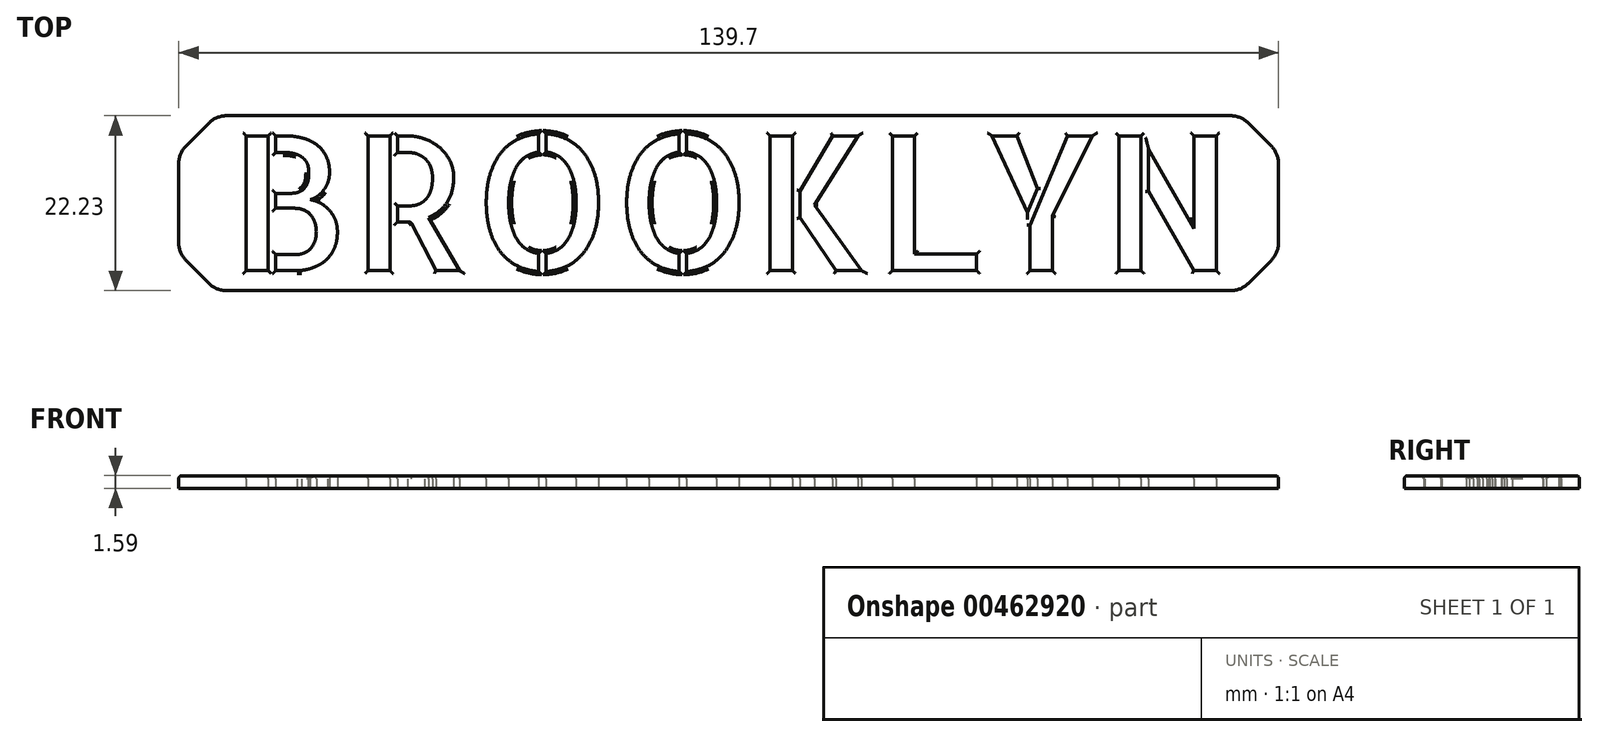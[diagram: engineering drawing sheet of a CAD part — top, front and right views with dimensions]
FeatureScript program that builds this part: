
annotation { "Feature Type Name" : "Feature", "Feature Type Description" : "" }
export const myFeature = defineFeature(function(context is Context, id is Id, definition is map)
    precondition{}
    {
        {
            var Q0;
            Q0=qCreatedBy(makeId("Top.planeOp"),FACE);
            var sketch = newSketch(context, id + "F0", { "sketchPlane" : qUnion([Q0])});
            skText(sketch, "E0", { "text": "BROOKLYN", "fontName": "AllertaStencil-Regular.ttf"});
            skLineSegment(sketch, "E1.bottom", {"start": v(-6.35, 19.68) * mm, "end": v(133.35, 19.68) * mm});
            skLineSegment(sketch, "E1.top", {"start": v(-6.35, -2.55) * mm, "end": v(133.35, -2.55) * mm});
            skLineSegment(sketch, "E1.left", {"start": v(-6.35, 19.68) * mm, "end": v(-6.35, -2.55) * mm});
            skLineSegment(sketch, "E1.right", {"start": v(133.35, 19.68) * mm, "end": v(133.35, -2.55) * mm});
            skLineSegment(sketch, "E2", {"start": v(63.5, 17.13) * mm, "end": v(63.5, 19.68) * mm, "construction": true});
            skLineSegment(sketch, "E3", {"start": v(63.5, -2.55) * mm, "end": v(63.5, 0) * mm, "construction": true});
            const initialGuessF0  = {"E0": [0, 0, 1, 0, 0.01713]};
            skSetInitialGuess(sketch, initialGuessF0);
            skSolve(sketch);
        }
        {
            var Q0;
            Q0 = qSketchRegion(id + "F0", true);
            extrude(context, id + "F1", {"entities" : qUnion([Q0]), "depth" : 1.59 * mm});
        }
        {
            var Q0;
            Q0=makeQuery(id+"F1.opExtrude","SWEPT_EDGE",EDGE,{"disambiguationData":[OSD([sQuery(id+"F0.wireOp",EDGE,"E1.bottom"),sQuery(id+"F0.wireOp",EDGE,"E1.right")])]});
            var Q1;
            Q1=makeQuery(id+"F1.opExtrude","SWEPT_EDGE",EDGE,{"disambiguationData":[OSD([sQuery(id+"F0.wireOp",EDGE,"E1.top"),sQuery(id+"F0.wireOp",EDGE,"E1.right")])]});
            var Q2;
            Q2=makeQuery(id+"F1.opExtrude","SWEPT_EDGE",EDGE,{"disambiguationData":[OSD([sQuery(id+"F0.wireOp",EDGE,"E1.top"),sQuery(id+"F0.wireOp",EDGE,"E1.left")])]});
            var Q3;
            Q3=makeQuery(id+"F1.opExtrude","SWEPT_EDGE",EDGE,{"disambiguationData":[OSD([sQuery(id+"F0.wireOp",EDGE,"E1.bottom"),sQuery(id+"F0.wireOp",EDGE,"E1.left")])]});
            chamfer(context, id + "F2", {"entities" : qUnion([Q0, Q1, Q2, Q3]), "width" : 4.76 * mm, "tangentPropagation" : true});
        }
        {
            var Q0;
            Q0=makeQuery(id+"F1.opExtrude","CAP_EDGE",EDGE,{"disambiguationData":[OSD([sQuery(id+"F0.wireOp",EDGE,"E0.sketch_text.stroke-179")])],"isStart":false});
            var Q1;
            Q1=makeQuery(id+"F1.opExtrude","CAP_EDGE",EDGE,{"disambiguationData":[OSD([sQuery(id+"F0.wireOp",EDGE,"E0.sketch_text.stroke-182")])],"isStart":false});
            var Q2;
            Q2=makeQuery(id+"F1.opExtrude","CAP_EDGE",EDGE,{"disambiguationData":[OSD([sQuery(id+"F0.wireOp",EDGE,"E0.sketch_text.stroke-181")])],"isStart":false});
            var Q3;
            Q3=makeQuery(id+"F1.opExtrude","CAP_EDGE",EDGE,{"disambiguationData":[OSD([sQuery(id+"F0.wireOp",EDGE,"E0.sketch_text.stroke-180")])],"isStart":false});
            fillet(context, id + "F3", {"entities" : qUnion([Q0, Q1, Q2, Q3]), "radius" : 0.38 * mm, "tangentPropagation" : true, "allowEdgeOverflow" : false});
        }
        {
            var Q0;
            Q0=makeQuery(id+"F1.opExtrude","CAP_EDGE",EDGE,{"disambiguationData":[OSD([sQuery(id+"F0.wireOp",EDGE,"E0.sketch_text.stroke-177")])],"isStart":false});
            var Q1;
            Q1=makeQuery(id+"F1.opExtrude","CAP_EDGE",EDGE,{"disambiguationData":[OSD([sQuery(id+"F0.wireOp",EDGE,"E0.sketch_text.stroke-175")])],"isStart":false});
            var Q2;
            Q2=makeQuery(id+"F1.opExtrude","CAP_EDGE",EDGE,{"disambiguationData":[OSD([sQuery(id+"F0.wireOp",EDGE,"E0.sketch_text.stroke-176")])],"isStart":false});
            var Q3;
            Q3=makeQuery(id+"F1.opExtrude","CAP_EDGE",EDGE,{"disambiguationData":[OSD([sQuery(id+"F0.wireOp",EDGE,"E0.sketch_text.stroke-178")])],"isStart":false});
            var Q4;
            Q4=makeQuery(id+"F1.opExtrude","CAP_EDGE",EDGE,{"disambiguationData":[OSD([sQuery(id+"F0.wireOp",EDGE,"E0.sketch_text.stroke-172")])],"isStart":false});
            var Q5;
            Q5=makeQuery(id+"F1.opExtrude","CAP_EDGE",EDGE,{"disambiguationData":[OSD([sQuery(id+"F0.wireOp",EDGE,"E0.sketch_text.stroke-173")])],"isStart":false});
            var Q6;
            Q6=makeQuery(id+"F1.opExtrude","CAP_EDGE",EDGE,{"disambiguationData":[OSD([sQuery(id+"F0.wireOp",EDGE,"E0.sketch_text.stroke-174")])],"isStart":false});
            var Q7;
            Q7=makeQuery(id+"F1.opExtrude","CAP_EDGE",EDGE,{"disambiguationData":[OSD([sQuery(id+"F0.wireOp",EDGE,"E0.sketch_text.stroke-163")])],"isStart":false});
            var Q8;
            Q8=makeQuery(id+"F1.opExtrude","CAP_EDGE",EDGE,{"disambiguationData":[OSD([sQuery(id+"F0.wireOp",EDGE,"E0.sketch_text.stroke-164")])],"isStart":false});
            var Q9;
            Q9=makeQuery(id+"F1.opExtrude","CAP_EDGE",EDGE,{"disambiguationData":[OSD([sQuery(id+"F0.wireOp",EDGE,"E0.sketch_text.stroke-165")])],"isStart":false});
            var Q10;
            Q10=makeQuery(id+"F1.opExtrude","CAP_EDGE",EDGE,{"disambiguationData":[OSD([sQuery(id+"F0.wireOp",EDGE,"E0.sketch_text.stroke-166")])],"isStart":false});
            var Q11;
            Q11=makeQuery(id+"F1.opExtrude","CAP_EDGE",EDGE,{"disambiguationData":[OSD([sQuery(id+"F0.wireOp",EDGE,"E0.sketch_text.stroke-167")])],"isStart":false});
            var Q12;
            Q12=makeQuery(id+"F1.opExtrude","CAP_EDGE",EDGE,{"disambiguationData":[OSD([sQuery(id+"F0.wireOp",EDGE,"E0.sketch_text.stroke-162")])],"isStart":false});
            var Q13;
            Q13=makeQuery(id+"F1.opExtrude","CAP_EDGE",EDGE,{"disambiguationData":[OSD([sQuery(id+"F0.wireOp",EDGE,"E0.sketch_text.stroke-168")])],"isStart":false});
            var Q14;
            Q14=makeQuery(id+"F1.opExtrude","CAP_EDGE",EDGE,{"disambiguationData":[OSD([sQuery(id+"F0.wireOp",EDGE,"E0.sketch_text.stroke-171")])],"isStart":false});
            var Q15;
            Q15=makeQuery(id+"F1.opExtrude","CAP_EDGE",EDGE,{"disambiguationData":[OSD([sQuery(id+"F0.wireOp",EDGE,"E0.sketch_text.stroke-170")])],"isStart":false});
            var Q16;
            Q16=makeQuery(id+"F1.opExtrude","CAP_EDGE",EDGE,{"disambiguationData":[OSD([sQuery(id+"F0.wireOp",EDGE,"E0.sketch_text.stroke-169")])],"isStart":false});
            fillet(context, id + "F4", {"entities" : qUnion([Q0, Q1, Q2, Q3, Q4, Q5, Q6, Q7, Q8, Q9, Q10, Q11, Q12, Q13, Q14, Q15, Q16]), "radius" : 0.38 * mm, "tangentPropagation" : true, "allowEdgeOverflow" : false});
        }
        {
            var Q0;
            Q0=makeQuery(id+"F1.opExtrude","CAP_EDGE",EDGE,{"disambiguationData":[OSD([sQuery(id+"F0.wireOp",EDGE,"E0.sketch_text.stroke-157")])],"isStart":false});
            var Q1;
            Q1=makeQuery(id+"F1.opExtrude","CAP_EDGE",EDGE,{"disambiguationData":[OSD([sQuery(id+"F0.wireOp",EDGE,"E0.sketch_text.stroke-156")])],"isStart":false});
            var Q2;
            Q2=makeQuery(id+"F1.opExtrude","CAP_EDGE",EDGE,{"disambiguationData":[OSD([sQuery(id+"F0.wireOp",EDGE,"E0.sketch_text.stroke-161")])],"isStart":false});
            var Q3;
            Q3=makeQuery(id+"F1.opExtrude","CAP_EDGE",EDGE,{"disambiguationData":[OSD([sQuery(id+"F0.wireOp",EDGE,"E0.sketch_text.stroke-160")])],"isStart":false});
            var Q4;
            Q4=makeQuery(id+"F1.opExtrude","CAP_EDGE",EDGE,{"disambiguationData":[OSD([sQuery(id+"F0.wireOp",EDGE,"E0.sketch_text.stroke-159")])],"isStart":false});
            var Q5;
            Q5=makeQuery(id+"F1.opExtrude","CAP_EDGE",EDGE,{"disambiguationData":[OSD([sQuery(id+"F0.wireOp",EDGE,"E0.sketch_text.stroke-158")])],"isStart":false});
            var Q6;
            Q6=makeQuery(id+"F1.opExtrude","CAP_EDGE",EDGE,{"disambiguationData":[OSD([sQuery(id+"F0.wireOp",EDGE,"E0.sketch_text.stroke-150")])],"isStart":false});
            var Q7;
            Q7=makeQuery(id+"F1.opExtrude","CAP_EDGE",EDGE,{"disambiguationData":[OSD([sQuery(id+"F0.wireOp",EDGE,"E0.sketch_text.stroke-149")])],"isStart":false});
            var Q8;
            Q8=makeQuery(id+"F1.opExtrude","CAP_EDGE",EDGE,{"disambiguationData":[OSD([sQuery(id+"F0.wireOp",EDGE,"E0.sketch_text.stroke-151")])],"isStart":false});
            var Q9;
            Q9=makeQuery(id+"F1.opExtrude","CAP_EDGE",EDGE,{"disambiguationData":[OSD([sQuery(id+"F0.wireOp",EDGE,"E0.sketch_text.stroke-155")])],"isStart":false});
            var Q10;
            Q10=makeQuery(id+"F1.opExtrude","CAP_EDGE",EDGE,{"disambiguationData":[OSD([sQuery(id+"F0.wireOp",EDGE,"E0.sketch_text.stroke-152")])],"isStart":false});
            var Q11;
            Q11=makeQuery(id+"F1.opExtrude","CAP_EDGE",EDGE,{"disambiguationData":[OSD([sQuery(id+"F0.wireOp",EDGE,"E0.sketch_text.stroke-153")])],"isStart":false});
            var Q12;
            Q12=makeQuery(id+"F1.opExtrude","CAP_EDGE",EDGE,{"disambiguationData":[OSD([sQuery(id+"F0.wireOp",EDGE,"E0.sketch_text.stroke-154")])],"isStart":false});
            var Q13;
            Q13=makeQuery(id+"F1.opExtrude","CAP_EDGE",EDGE,{"disambiguationData":[OSD([sQuery(id+"F0.wireOp",EDGE,"E0.sketch_text.stroke-145")])],"isStart":false});
            var Q14;
            Q14=makeQuery(id+"F1.opExtrude","CAP_EDGE",EDGE,{"disambiguationData":[OSD([sQuery(id+"F0.wireOp",EDGE,"E0.sketch_text.stroke-147")])],"isStart":false});
            var Q15;
            Q15=makeQuery(id+"F1.opExtrude","CAP_EDGE",EDGE,{"disambiguationData":[OSD([sQuery(id+"F0.wireOp",EDGE,"E0.sketch_text.stroke-148")])],"isStart":false});
            var Q16;
            Q16=makeQuery(id+"F1.opExtrude","CAP_EDGE",EDGE,{"disambiguationData":[OSD([sQuery(id+"F0.wireOp",EDGE,"E0.sketch_text.stroke-146")])],"isStart":false});
            fillet(context, id + "F5", {"entities" : qUnion([Q0, Q1, Q2, Q3, Q4, Q5, Q6, Q7, Q8, Q9, Q10, Q11, Q12, Q13, Q14, Q15, Q16]), "radius" : 0.38 * mm, "tangentPropagation" : true, "allowEdgeOverflow" : false});
        }
        {
            var Q0;
            Q0=makeQuery(id+"F1.opExtrude","CAP_EDGE",EDGE,{"disambiguationData":[OSD([sQuery(id+"F0.wireOp",EDGE,"E0.sketch_text.stroke-42")])],"isStart":false});
            var Q1;
            Q1=makeQuery(id+"F1.opExtrude","CAP_EDGE",EDGE,{"disambiguationData":[OSD([sQuery(id+"F0.wireOp",EDGE,"E0.sketch_text.stroke-40")])],"isStart":false});
            var Q2;
            Q2=makeQuery(id+"F1.opExtrude","CAP_EDGE",EDGE,{"disambiguationData":[OSD([sQuery(id+"F0.wireOp",EDGE,"E0.sketch_text.stroke-39")])],"isStart":false});
            var Q3;
            Q3=makeQuery(id+"F1.opExtrude","CAP_EDGE",EDGE,{"disambiguationData":[OSD([sQuery(id+"F0.wireOp",EDGE,"E0.sketch_text.stroke-41")])],"isStart":false});
            var Q4;
            Q4=makeQuery(id+"F1.opExtrude","CAP_EDGE",EDGE,{"disambiguationData":[OSD([sQuery(id+"F0.wireOp",EDGE,"E0.sketch_text.stroke-46")])],"isStart":false});
            var Q5;
            Q5=makeQuery(id+"F1.opExtrude","CAP_EDGE",EDGE,{"disambiguationData":[OSD([sQuery(id+"F0.wireOp",EDGE,"E0.sketch_text.stroke-43")])],"isStart":false});
            var Q6;
            Q6=makeQuery(id+"F1.opExtrude","CAP_EDGE",EDGE,{"disambiguationData":[OSD([sQuery(id+"F0.wireOp",EDGE,"E0.sketch_text.stroke-44")])],"isStart":false});
            var Q7;
            Q7=makeQuery(id+"F1.opExtrude","CAP_EDGE",EDGE,{"disambiguationData":[OSD([sQuery(id+"F0.wireOp",EDGE,"E0.sketch_text.stroke-45")])],"isStart":false});
            fillet(context, id + "F6", {"entities" : qUnion([Q0, Q1, Q2, Q3, Q4, Q5, Q6, Q7]), "radius" : 0.38 * mm, "tangentPropagation" : true, "allowEdgeOverflow" : false});
        }
        {
            var Q0;
            Q0=makeQuery(id+"F1.opExtrude","CAP_EDGE",EDGE,{"disambiguationData":[OSD([sQuery(id+"F0.wireOp",EDGE,"E0.sketch_text.stroke-17")])],"isStart":false});
            var Q1;
            Q1=makeQuery(id+"F1.opExtrude","CAP_EDGE",EDGE,{"disambiguationData":[OSD([sQuery(id+"F0.wireOp",EDGE,"E0.sketch_text.stroke-11")])],"isStart":false});
            var Q2;
            Q2=makeQuery(id+"F1.opExtrude","CAP_EDGE",EDGE,{"disambiguationData":[OSD([sQuery(id+"F0.wireOp",EDGE,"E0.sketch_text.stroke-10")])],"isStart":false});
            var Q3;
            Q3=makeQuery(id+"F1.opExtrude","CAP_EDGE",EDGE,{"disambiguationData":[OSD([sQuery(id+"F0.wireOp",EDGE,"E0.sketch_text.stroke-37")])],"isStart":false});
            var Q4;
            Q4=makeQuery(id+"F1.opExtrude","CAP_EDGE",EDGE,{"disambiguationData":[OSD([sQuery(id+"F0.wireOp",EDGE,"E0.sketch_text.stroke-29")])],"isStart":false});
            var Q5;
            Q5=makeQuery(id+"F1.opExtrude","CAP_EDGE",EDGE,{"disambiguationData":[OSD([sQuery(id+"F0.wireOp",EDGE,"E0.sketch_text.stroke-28")])],"isStart":false});
            var Q6;
            Q6=makeQuery(id+"F1.opExtrude","CAP_EDGE",EDGE,{"disambiguationData":[OSD([sQuery(id+"F0.wireOp",EDGE,"E0.sketch_text.stroke-18")])],"isStart":false});
            fillet(context, id + "F7", {"entities" : qUnion([Q0, Q1, Q2, Q3, Q4, Q5, Q6]), "radius" : 0.38 * mm, "tangentPropagation" : true, "allowEdgeOverflow" : false});
        }
        {
            var Q0;
            Q0=makeQuery(id+"F1.opExtrude","CAP_EDGE",EDGE,{"disambiguationData":[OSD([sQuery(id+"F0.wireOp",EDGE,"E0.sketch_text.stroke-53")])],"isStart":false});
            var Q1;
            Q1=makeQuery(id+"F1.opExtrude","CAP_EDGE",EDGE,{"disambiguationData":[OSD([sQuery(id+"F0.wireOp",EDGE,"E0.sketch_text.stroke-54")])],"isStart":false});
            var Q2;
            Q2=makeQuery(id+"F1.opExtrude","CAP_EDGE",EDGE,{"disambiguationData":[OSD([sQuery(id+"F0.wireOp",EDGE,"E0.sketch_text.stroke-64")])],"isStart":false});
            var Q3;
            Q3=makeQuery(id+"F1.opExtrude","CAP_EDGE",EDGE,{"disambiguationData":[OSD([sQuery(id+"F0.wireOp",EDGE,"E0.sketch_text.stroke-65")])],"isStart":false});
            var Q4;
            Q4=makeQuery(id+"F1.opExtrude","CAP_EDGE",EDGE,{"disambiguationData":[OSD([sQuery(id+"F0.wireOp",EDGE,"E0.sketch_text.stroke-72")])],"isStart":false});
            var Q5;
            Q5=makeQuery(id+"F1.opExtrude","CAP_EDGE",EDGE,{"disambiguationData":[OSD([sQuery(id+"F0.wireOp",EDGE,"E0.sketch_text.stroke-47")])],"isStart":false});
            var Q6;
            Q6=makeQuery(id+"F1.opExtrude","CAP_EDGE",EDGE,{"disambiguationData":[OSD([sQuery(id+"F0.wireOp",EDGE,"E0.sketch_text.stroke-48")])],"isStart":false});
            fillet(context, id + "F8", {"entities" : qUnion([Q0, Q1, Q2, Q3, Q4, Q5, Q6]), "radius" : 0.38 * mm, "tangentPropagation" : true, "allowEdgeOverflow" : false});
        }
        {
            var Q0;
            Q0=makeQuery(id+"F1.opExtrude","CAP_EDGE",EDGE,{"disambiguationData":[OSD([sQuery(id+"F0.wireOp",EDGE,"E0.sketch_text.stroke-52")])],"isStart":false});
            var Q1;
            Q1=makeQuery(id+"F1.opExtrude","CAP_EDGE",EDGE,{"disambiguationData":[OSD([sQuery(id+"F0.wireOp",EDGE,"E0.sketch_text.stroke-76")])],"isStart":false});
            var Q2;
            Q2=makeQuery(id+"F1.opExtrude","CAP_EDGE",EDGE,{"disambiguationData":[OSD([sQuery(id+"F0.wireOp",EDGE,"E0.sketch_text.stroke-86")])],"isStart":false});
            var Q3;
            Q3=makeQuery(id+"F1.opExtrude","CAP_EDGE",EDGE,{"disambiguationData":[OSD([sQuery(id+"F0.wireOp",EDGE,"E0.sketch_text.stroke-85")])],"isStart":false});
            var Q4;
            Q4=makeQuery(id+"F1.opExtrude","CAP_EDGE",EDGE,{"disambiguationData":[OSD([sQuery(id+"F0.wireOp",EDGE,"E0.sketch_text.stroke-81")])],"isStart":false});
            var Q5;
            Q5=makeQuery(id+"F1.opExtrude","CAP_EDGE",EDGE,{"disambiguationData":[OSD([sQuery(id+"F0.wireOp",EDGE,"E0.sketch_text.stroke-77")])],"isStart":false});
            var Q6;
            Q6=makeQuery(id+"F1.opExtrude","CAP_EDGE",EDGE,{"disambiguationData":[OSD([sQuery(id+"F0.wireOp",EDGE,"E0.sketch_text.stroke-108")])],"isStart":false});
            var Q7;
            Q7=makeQuery(id+"F1.opExtrude","CAP_EDGE",EDGE,{"disambiguationData":[OSD([sQuery(id+"F0.wireOp",EDGE,"E0.sketch_text.stroke-107")])],"isStart":false});
            var Q8;
            Q8=makeQuery(id+"F1.opExtrude","CAP_EDGE",EDGE,{"disambiguationData":[OSD([sQuery(id+"F0.wireOp",EDGE,"E0.sketch_text.stroke-103")])],"isStart":false});
            var Q9;
            Q9=makeQuery(id+"F1.opExtrude","CAP_EDGE",EDGE,{"disambiguationData":[OSD([sQuery(id+"F0.wireOp",EDGE,"E0.sketch_text.stroke-99")])],"isStart":false});
            var Q10;
            Q10=makeQuery(id+"F1.opExtrude","CAP_EDGE",EDGE,{"disambiguationData":[OSD([sQuery(id+"F0.wireOp",EDGE,"E0.sketch_text.stroke-98")])],"isStart":false});
            fillet(context, id + "F9", {"entities" : qUnion([Q0, Q1, Q2, Q3, Q4, Q5, Q6, Q7, Q8, Q9, Q10]), "radius" : 0.38 * mm, "tangentPropagation" : true, "allowEdgeOverflow" : false});
        }
        {
            var Q0;
            Q0=makeQuery(id+"F1.opExtrude","CAP_EDGE",EDGE,{"disambiguationData":[OSD([sQuery(id+"F0.wireOp",EDGE,"E0.sketch_text.stroke-112")])],"isStart":false});
            var Q1;
            Q1=makeQuery(id+"F1.opExtrude","CAP_EDGE",EDGE,{"disambiguationData":[OSD([sQuery(id+"F0.wireOp",EDGE,"E0.sketch_text.stroke-122")])],"isStart":false});
            var Q2;
            Q2=makeQuery(id+"F1.opExtrude","CAP_EDGE",EDGE,{"disambiguationData":[OSD([sQuery(id+"F0.wireOp",EDGE,"E0.sketch_text.stroke-121")])],"isStart":false});
            var Q3;
            Q3=makeQuery(id+"F1.opExtrude","CAP_EDGE",EDGE,{"disambiguationData":[OSD([sQuery(id+"F0.wireOp",EDGE,"E0.sketch_text.stroke-117")])],"isStart":false});
            var Q4;
            Q4=makeQuery(id+"F1.opExtrude","CAP_EDGE",EDGE,{"disambiguationData":[OSD([sQuery(id+"F0.wireOp",EDGE,"E0.sketch_text.stroke-113")])],"isStart":false});
            var Q5;
            Q5=makeQuery(id+"F1.opExtrude","CAP_EDGE",EDGE,{"disambiguationData":[OSD([sQuery(id+"F0.wireOp",EDGE,"E0.sketch_text.stroke-144")])],"isStart":false});
            var Q6;
            Q6=makeQuery(id+"F1.opExtrude","CAP_EDGE",EDGE,{"disambiguationData":[OSD([sQuery(id+"F0.wireOp",EDGE,"E0.sketch_text.stroke-143")])],"isStart":false});
            var Q7;
            Q7=makeQuery(id+"F1.opExtrude","CAP_EDGE",EDGE,{"disambiguationData":[OSD([sQuery(id+"F0.wireOp",EDGE,"E0.sketch_text.stroke-139")])],"isStart":false});
            var Q8;
            Q8=makeQuery(id+"F1.opExtrude","CAP_EDGE",EDGE,{"disambiguationData":[OSD([sQuery(id+"F0.wireOp",EDGE,"E0.sketch_text.stroke-135")])],"isStart":false});
            var Q9;
            Q9=makeQuery(id+"F1.opExtrude","CAP_EDGE",EDGE,{"disambiguationData":[OSD([sQuery(id+"F0.wireOp",EDGE,"E0.sketch_text.stroke-134")])],"isStart":false});
            fillet(context, id + "F10", {"entities" : qUnion([Q0, Q1, Q2, Q3, Q4, Q5, Q6, Q7, Q8, Q9]), "radius" : 0.38 * mm, "tangentPropagation" : true, "allowEdgeOverflow" : false});
        }
        {
            var Q0;
            {var subQ0=sQuery(id+"F0.wireOp",EDGE,"E1.bottom");Q0=makeQuery(id+"F2.opChamfer","BLEND_EDGE",EDGE,{"blendedFrom":[makeQuery(id+"F1.opExtrude","SWEPT_EDGE",EDGE,{"disambiguationData":[OSD([subQ0,sQuery(id+"F0.wireOp",EDGE,"E1.right")])]}),makeQuery(id+"F1.opExtrude","SWEPT_FACE",FACE,{"disambiguationData":[OSD([subQ0])]})],"blendedInto":[makeQuery(id+"F1.opExtrude","SWEPT_FACE",FACE,{"disambiguationData":[OSD([subQ0])]})]});}
            var Q1;
            {var subQ0=sQuery(id+"F0.wireOp",EDGE,"E1.right");Q1=makeQuery(id+"F2.opChamfer","BLEND_EDGE",EDGE,{"blendedFrom":[makeQuery(id+"F1.opExtrude","SWEPT_EDGE",EDGE,{"disambiguationData":[OSD([sQuery(id+"F0.wireOp",EDGE,"E1.bottom"),subQ0])]}),makeQuery(id+"F1.opExtrude","SWEPT_FACE",FACE,{"disambiguationData":[OSD([subQ0])]})],"blendedInto":[makeQuery(id+"F1.opExtrude","SWEPT_FACE",FACE,{"disambiguationData":[OSD([subQ0])]})]});}
            var Q2;
            {var subQ0=sQuery(id+"F0.wireOp",EDGE,"E1.right");Q2=makeQuery(id+"F2.opChamfer","BLEND_EDGE",EDGE,{"blendedFrom":[makeQuery(id+"F1.opExtrude","SWEPT_EDGE",EDGE,{"disambiguationData":[OSD([sQuery(id+"F0.wireOp",EDGE,"E1.top"),subQ0])]}),makeQuery(id+"F1.opExtrude","SWEPT_FACE",FACE,{"disambiguationData":[OSD([subQ0])]})],"blendedInto":[makeQuery(id+"F1.opExtrude","SWEPT_FACE",FACE,{"disambiguationData":[OSD([subQ0])]})]});}
            var Q3;
            {var subQ0=sQuery(id+"F0.wireOp",EDGE,"E1.top");Q3=makeQuery(id+"F2.opChamfer","BLEND_EDGE",EDGE,{"blendedFrom":[makeQuery(id+"F1.opExtrude","SWEPT_EDGE",EDGE,{"disambiguationData":[OSD([subQ0,sQuery(id+"F0.wireOp",EDGE,"E1.right")])]}),makeQuery(id+"F1.opExtrude","SWEPT_FACE",FACE,{"disambiguationData":[OSD([subQ0])]})],"blendedInto":[makeQuery(id+"F1.opExtrude","SWEPT_FACE",FACE,{"disambiguationData":[OSD([subQ0])]})]});}
            var Q4;
            {var subQ0=sQuery(id+"F0.wireOp",EDGE,"E1.top");Q4=makeQuery(id+"F2.opChamfer","BLEND_EDGE",EDGE,{"blendedFrom":[makeQuery(id+"F1.opExtrude","SWEPT_EDGE",EDGE,{"disambiguationData":[OSD([subQ0,sQuery(id+"F0.wireOp",EDGE,"E1.left")])]}),makeQuery(id+"F1.opExtrude","SWEPT_FACE",FACE,{"disambiguationData":[OSD([subQ0])]})],"blendedInto":[makeQuery(id+"F1.opExtrude","SWEPT_FACE",FACE,{"disambiguationData":[OSD([subQ0])]})]});}
            var Q5;
            {var subQ0=sQuery(id+"F0.wireOp",EDGE,"E1.left");Q5=makeQuery(id+"F2.opChamfer","BLEND_EDGE",EDGE,{"blendedFrom":[makeQuery(id+"F1.opExtrude","SWEPT_EDGE",EDGE,{"disambiguationData":[OSD([sQuery(id+"F0.wireOp",EDGE,"E1.top"),subQ0])]}),makeQuery(id+"F1.opExtrude","SWEPT_FACE",FACE,{"disambiguationData":[OSD([subQ0])]})],"blendedInto":[makeQuery(id+"F1.opExtrude","SWEPT_FACE",FACE,{"disambiguationData":[OSD([subQ0])]})]});}
            var Q6;
            {var subQ0=sQuery(id+"F0.wireOp",EDGE,"E1.left");Q6=makeQuery(id+"F2.opChamfer","BLEND_EDGE",EDGE,{"blendedFrom":[makeQuery(id+"F1.opExtrude","SWEPT_EDGE",EDGE,{"disambiguationData":[OSD([sQuery(id+"F0.wireOp",EDGE,"E1.bottom"),subQ0])]}),makeQuery(id+"F1.opExtrude","SWEPT_FACE",FACE,{"disambiguationData":[OSD([subQ0])]})],"blendedInto":[makeQuery(id+"F1.opExtrude","SWEPT_FACE",FACE,{"disambiguationData":[OSD([subQ0])]})]});}
            var Q7;
            {var subQ0=sQuery(id+"F0.wireOp",EDGE,"E1.bottom");Q7=makeQuery(id+"F2.opChamfer","BLEND_EDGE",EDGE,{"blendedFrom":[makeQuery(id+"F1.opExtrude","SWEPT_EDGE",EDGE,{"disambiguationData":[OSD([subQ0,sQuery(id+"F0.wireOp",EDGE,"E1.left")])]}),makeQuery(id+"F1.opExtrude","SWEPT_FACE",FACE,{"disambiguationData":[OSD([subQ0])]})],"blendedInto":[makeQuery(id+"F1.opExtrude","SWEPT_FACE",FACE,{"disambiguationData":[OSD([subQ0])]})]});}
            fillet(context, id + "F11", {"entities" : qUnion([Q0, Q1, Q2, Q3, Q4, Q5, Q6, Q7]), "radius" : 3.17 * mm, "tangentPropagation" : true, "allowEdgeOverflow" : false});
        }
        {
            var Q0;
            Q0=makeQuery(id+"F1.opExtrude","CAP_EDGE",EDGE,{"disambiguationData":[OSD([sQuery(id+"F0.wireOp",EDGE,"E1.bottom")])],"isStart":false});
            fillet(context, id + "F12", {"entities" : qUnion([Q0]), "radius" : 0.38 * mm, "tangentPropagation" : true, "allowEdgeOverflow" : false});
        }
    });
